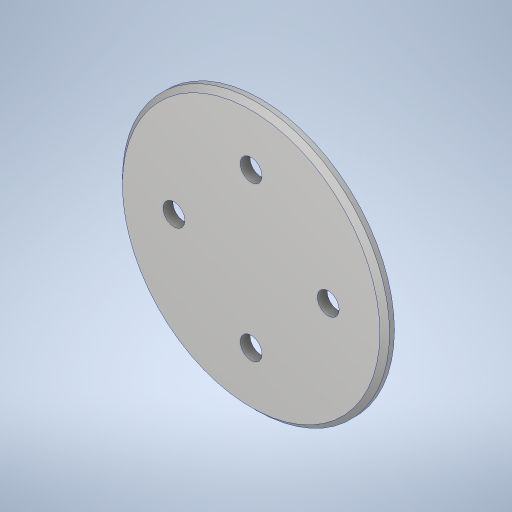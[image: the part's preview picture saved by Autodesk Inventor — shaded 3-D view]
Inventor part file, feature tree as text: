
AUTODESK INVENTOR PART (.ipt)
format: ipt  version: 2023.3 (Build 273359000, 359)  size: 252,416 bytes
history: native  units: in
note: dims shown in document units (in); Inventor stores cm internally (conversion verified against a paired STEP export)
features: sketch x2, extrude x1, chamfer x1, hole x1
ambient origin geometry x8: Origin, YZ Plane, XZ Plane, XY Plane, X Axis, Y Axis, Z Axis, Center Point
bodies: Solid1 (feature_tree)
feature tree (5):
  extrude  "Extrusion1"  Depth=0.0787in TaperAngle=0.0deg
  chamfer  "Chamfer1"  Distance=0.0394in Angle=45.0deg
  hole  "Hole1"  [1 undecoded]
  sketch  "Sketch1"  dims[d0=2.1654in d1=0.0787in d2=0.0in d3=0.0394in d4=0.125in d5=45.0deg]
  sketch  "Sketch2"  dims[d6=1.25in d7=1.5748in d9=360.0deg d11=0.177in d12=0.75in d13=0.332in d14=0.25in d15=0.5635in d16=1.0in d17=0.8108in]
note: 1 required parameter value undecoded (feature->parameter linkage not recoverable at this tier; creation-order binding heuristic only, values carry confidence <= 0.55)
